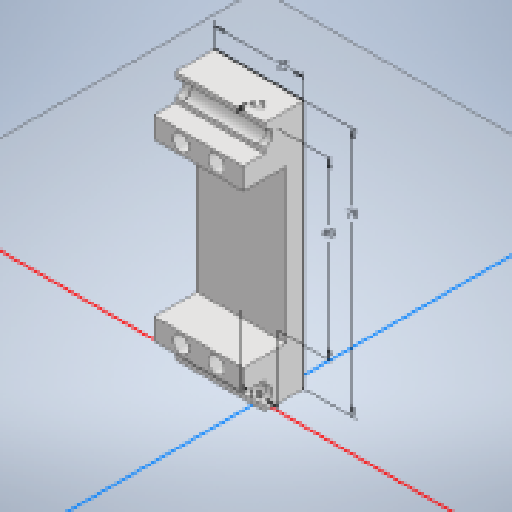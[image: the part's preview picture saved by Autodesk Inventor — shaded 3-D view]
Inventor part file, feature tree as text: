
AUTODESK INVENTOR PART (.ipt)
format: ipt  version: 2025.2 (Build 292293000, 293)  size: 211,968 bytes
history: native  units: mm
features: extrude x5, sketch x4, mirror x1
ambient origin geometry x8: Origin, YZ Plane, XZ Plane, XY Plane, X Axis, Y Axis, Z Axis, Center Point
bodies: Solid1 (feature_tree)
feature tree (10):
  sketch  "Sketch1"  dims[d0=4.5mm d1=10.0mm]
  extrude  "Extrusion1"  Depth=10.0mm
  sketch  "Sketch2"  dims[d4=70.0mm d5=5.0mm d6=0.0mm]
  extrude  "Extrusion2"  Depth=25.0mm
  extrude  "Extrusion3"  Depth=5.0mm TaperAngle=0.0deg
  extrude  "Extrusion4"  Depth=7.5mm
  mirror  "Mirror1"
  extrude  "Extrusion5"  Depth=5.0mm
  sketch  "Sketch3"  dims[d7=6.0mm d8=7.5mm d9=5.0mm d10=5.0mm d11=0.0mm d12=6.0mm d13=12.0mm d14=49.0mm d15=0.0mm d16=0.2mm d17=2.0mm d18=0.0mm d19=5.5mm d20=20.0mm d22=49.0mm d23=20.0mm d25=10.0mm d28=2.8mm d29=0.0mm]
  sketch  "Sketch Rectangular Pattern1"  dims[d2=49.0mm d3=25.0mm]
